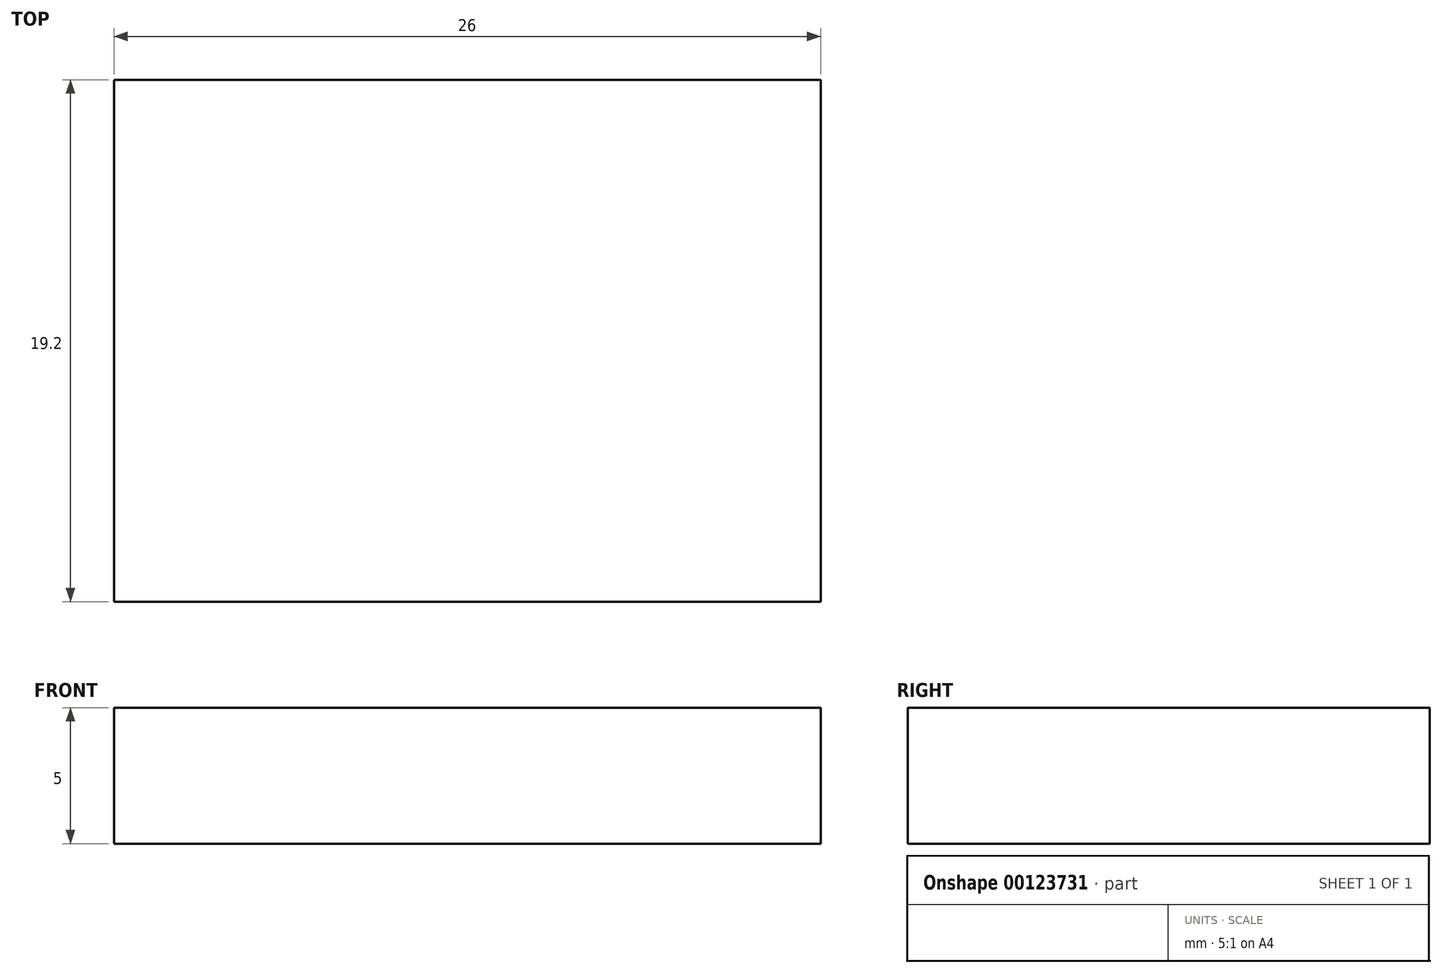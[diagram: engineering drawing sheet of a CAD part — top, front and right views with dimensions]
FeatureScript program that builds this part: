
annotation { "Feature Type Name" : "Feature", "Feature Type Description" : "" }
export const myFeature = defineFeature(function(context is Context, id is Id, definition is map)
    precondition{}
    {
        {
            var Q0;
            Q0=qCreatedBy(makeId("Top.planeOp"),FACE);
            var sketch = newSketch(context, id + "F0", { "sketchPlane" : qUnion([Q0])});
            skLineSegment(sketch, "E0.bottom", {"start": v(0, 19.07) * mm, "end": v(26, 19.07) * mm});
            skLineSegment(sketch, "E0.top", {"start": v(0, -0.13) * mm, "end": v(26, -0.13) * mm});
            skLineSegment(sketch, "E0.left", {"start": v(0, 19.07) * mm, "end": v(0, -0.13) * mm});
            skLineSegment(sketch, "E0.right", {"start": v(26, 19.07) * mm, "end": v(26, -0.13) * mm});
            skSolve(sketch);
        }
        {
            var Q0;
            Q0=makeQuery(id+"F0.imprint","IMPRINT",FACE,{"disambiguationData":[TD([[makeQuery(id+"F0.imprint","IMPRINT",EDGE,{"derivedFrom":sQuery(id+"F0.wireOp",EDGE,"E0.bottom")}),-1.0]])]});
            extrude(context, id + "F1", {"entities" : qUnion([Q0]), "depth" : 5 * mm});
        }
    });
